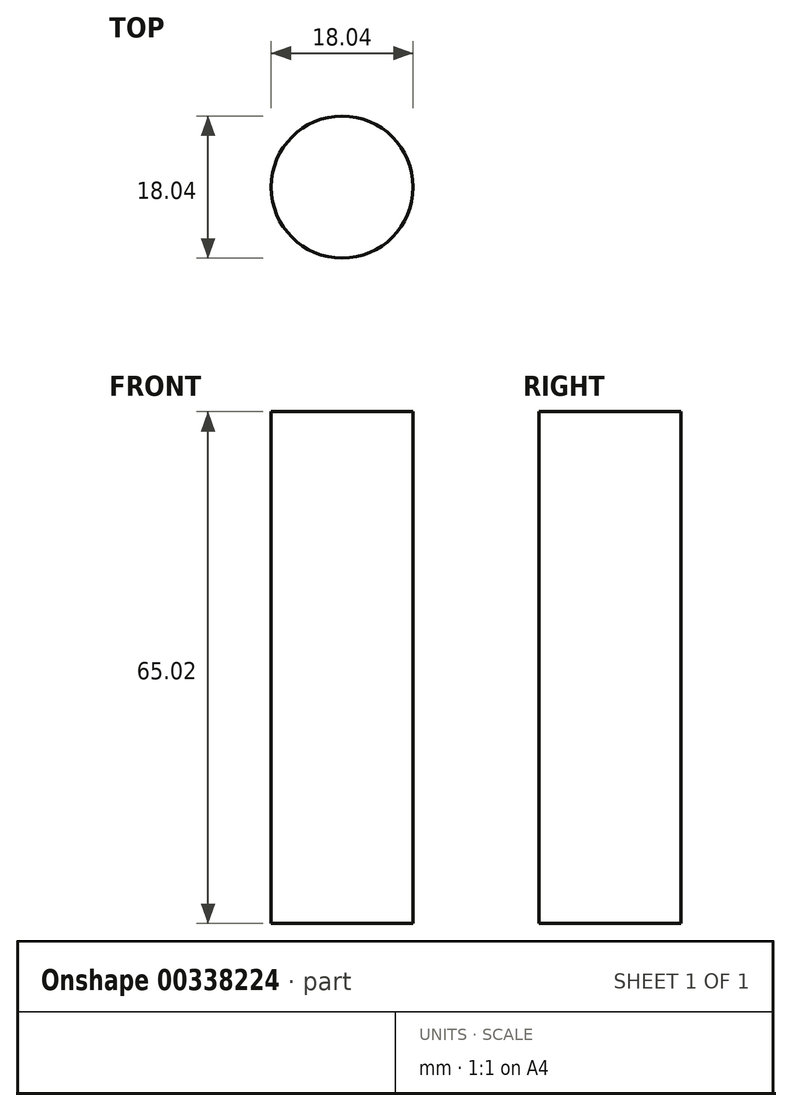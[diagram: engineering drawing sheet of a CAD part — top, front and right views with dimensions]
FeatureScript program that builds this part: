
annotation { "Feature Type Name" : "Feature", "Feature Type Description" : "" }
export const myFeature = defineFeature(function(context is Context, id is Id, definition is map)
    precondition{}
    {
        {
            var Q0;
            Q0=qCreatedBy(makeId("Top.planeOp"),FACE);
            var sketch = newSketch(context, id + "F0", { "sketchPlane" : qUnion([Q0])});
            skCircle(sketch, "E0", {"center": v(0, 0) * mm, "radius": 9.02 * mm});
            skSolve(sketch);
        }
        {
            var Q0;
            Q0 = qSketchRegion(id + "F0", true);
            extrude(context, id + "F1", {"entities" : qUnion([Q0]), "depth" : 65.02 * mm});
        }
    });
